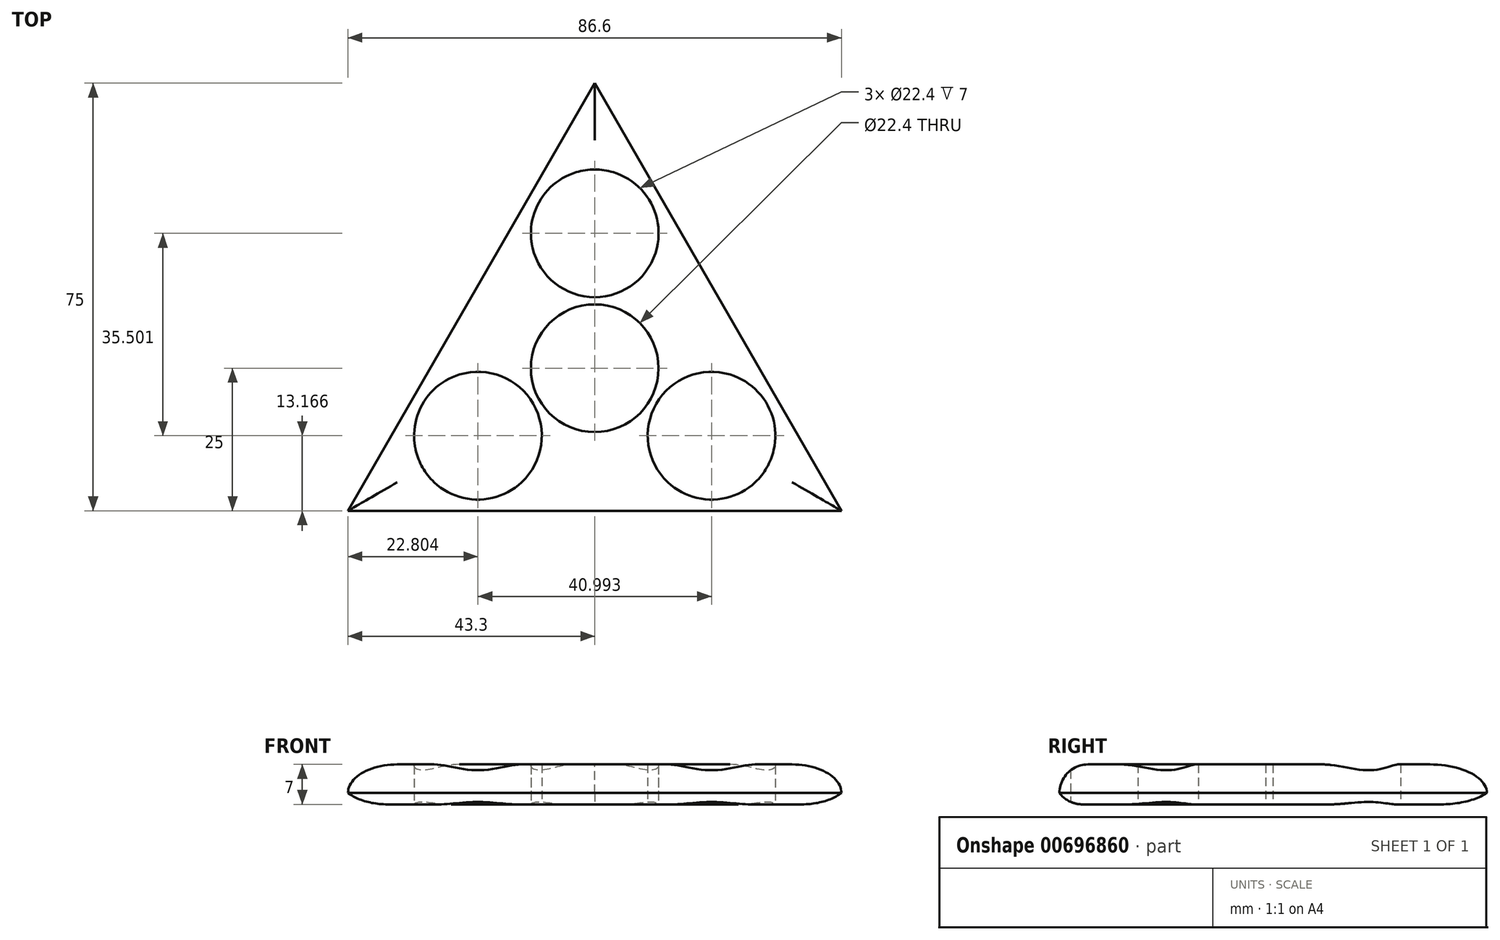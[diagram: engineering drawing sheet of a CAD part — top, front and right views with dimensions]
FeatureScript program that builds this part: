
annotation { "Feature Type Name" : "Feature", "Feature Type Description" : "" }
export const myFeature = defineFeature(function(context is Context, id is Id, definition is map)
    precondition{}
    {
        {
            var Q0;
            Q0=qCreatedBy(makeId("Top.planeOp"),FACE);
            var sketch = newSketch(context, id + "F0", { "sketchPlane" : qUnion([Q0])});
            skPoint(sketch, "E0.center", {"position": v(0, 0) * mm});
            skCircle(sketch, "E1", {"center": v(0, 0) * mm, "radius": 11.2 * mm});
            skLineSegment(sketch, "E2", {"start": v(0, 50) * mm, "end": v(-43.3, -25) * mm});
            skLineSegment(sketch, "E3", {"start": v(43.3, -25) * mm, "end": v(0, 50) * mm});
            skLineSegment(sketch, "E4", {"start": v(43.3, -25) * mm, "end": v(-43.3, -25) * mm});
            skCircle(sketch, "E5", {"center": v(0, 23.67) * mm, "radius": 11.2 * mm});
            skCircle(sketch, "E6.1.0", {"center": v(-20.5, -11.83) * mm, "radius": 11.2 * mm});
            skCircle(sketch, "E6.2.0", {"center": v(20.5, -11.83) * mm, "radius": 11.2 * mm});
            skSolve(sketch);
        }
        {
            var Q0;
            Q0 = qSketchRegion(id + "F0", true);
            extrude(context, id + "F1", {"entities" : qUnion([Q0]), "depth" : 7 * mm, "offsetDistance" : 25 * mm});
        }
        {
            var Q0;
            Q0=makeQuery(id+"F1.opExtrude","CAP_EDGE",EDGE,{"disambiguationData":[OSD([sQuery(id+"F0.wireOp",EDGE,"E2")])],"isStart":false});
            var Q1;
            Q1=makeQuery(id+"F1.opExtrude","CAP_EDGE",EDGE,{"disambiguationData":[OSD([sQuery(id+"F0.wireOp",EDGE,"E4")])],"isStart":false});
            var Q2;
            Q2=makeQuery(id+"F1.opExtrude","CAP_EDGE",EDGE,{"disambiguationData":[OSD([sQuery(id+"F0.wireOp",EDGE,"E3")])],"isStart":false});
            fillet(context, id + "F2", {"entities" : qUnion([Q0, Q1, Q2]), "radius" : 5 * mm, "tangentPropagation" : true, "allowEdgeOverflow" : false});
        }
        {
            var Q0;
            Q0=makeQuery(id+"F1.opExtrude","CAP_EDGE",EDGE,{"disambiguationData":[OSD([sQuery(id+"F0.wireOp",EDGE,"E3")])],"isStart":true});
            var Q1;
            Q1=makeQuery(id+"F1.opExtrude","CAP_EDGE",EDGE,{"disambiguationData":[OSD([sQuery(id+"F0.wireOp",EDGE,"E4")])],"isStart":true});
            var Q2;
            Q2=makeQuery(id+"F1.opExtrude","CAP_EDGE",EDGE,{"disambiguationData":[OSD([sQuery(id+"F0.wireOp",EDGE,"E2")])],"isStart":true});
            fillet(context, id + "F3", {"entities" : qUnion([Q0, Q1, Q2]), "radius" : 5 * mm, "tangentPropagation" : true, "allowEdgeOverflow" : false});
        }
    });
